# Revit family: Haworth_XSeries_Bookcase
name_source: partatom
category: Furniture Systems
revit_build: Autodesk Revit 2018 (Build: 20170223_1515(x64)
units: mm (PartAtom-declared; Revit-internal decimal feet)

## family parameters
Always vertical = Yes
Cut with Voids When Loaded = No
OmniClass Number = 23.40.70.14.64.21
OmniClass Title = Systems Furniture
Part Type = Normal
Room Calculation Point = No
Round Connector Dimension = Use Diameter
Shared = No
Work Plane-Based = No

## types (12) — shared parameters
Actual Depth = 14"
Assembly Code = E2020200
Custom Size = No
Description = Haworth XSeries Bookcase
Drawer Depth = 12 1/2"
Manufacturer = Haworth
Max # of Shelves = 4
Max. Height = 63 1/2"
Max. Width = 47 7/8"
Min. Height = 27 1/2"
Min. Width = 29 7/8"
Model = JBCS
Revision Number = 6
Size = Verify Final Dim. w/ Haworth
Standard Widths = 30, 36, 42 in.
Sustainability Info = https://www.haworth.com
URL = http://www.haworth.com
URL - Product = https://www.haworth.com
Warranty = http://www.haworth.com

## per-type parameters (varying)
| type | # of Shelves | Actaul # of Shelves | Actual Height | Actual Width | Cabinet Height | Drawer Width | Shelf Spacing | Shelves | Single Shelf | Width |
| 14d 36w 27h | 1 | 2 | 27 1/2" | 35 7/8" | 27 1/2" | 34 3/8" | 8 1/8" | No | Yes | 36" |
| 14d 36w 51h | 3 | 3 | 51 1/2" | 35 7/8" | 51 1/2" | 34 3/8" | 12 3/32" | Yes | No | 36" |
| 14d 36w 63h | 4 | 4 | 63 1/2" | 35 7/8" | 63 1/2" | 34 3/8" | 12 19/256" | Yes | No | 36" |
| 14d 30w 27h | 1 | 2 | 27 1/2" | 29 7/8" | 27 1/2" | 28 3/8" | 8 1/8" | No | Yes | 30" |
| 14d 30w 51h | 3 | 3 | 51 1/2" | 29 7/8" | 51 1/2" | 28 3/8" | 12 3/32" | Yes | No | 30" |
| 14d 30w 63h | 4 | 4 | 63 1/2" | 29 7/8" | 63 1/2" | 28 3/8" | 12 19/256" | Yes | No | 30" |
| 14d 42w 63h | 4 | 4 | 63 1/2" | 41 7/8" | 63 1/2" | 40 3/8" | 12 19/256" | Yes | No | 42" |
| 14d 42w 51h | 3 | 3 | 51 1/2" | 41 7/8" | 51 1/2" | 40 3/8" | 12 3/32" | Yes | No | 42" |
| 14d 42w 27h | 1 | 2 | 27 1/2" | 41 7/8" | 27 1/2" | 40 3/8" | 8 1/8" | No | Yes | 42" |
| 14d 30w 39h | 2 | 2 | 39 1/2" | 29 7/8" | 39 1/2" | 28 3/8" | 12 1/8" | Yes | No | 30" |
| 14d 36w 39h | 2 | 2 | 39 1/2" | 35 7/8" | 39 1/2" | 34 3/8" | 12 1/8" | Yes | No | 36" |
| 14d 42w 39h | 2 | 2 | 39 1/2" | 41 7/8" | 39 1/2" | 40 3/8" | 12 1/8" | Yes | No | 42" |

## geometry (parser evidence)
native form markers: Sweep x7
no freeform markers — native parametric forms only
